# Revit family: Towel_Ring-DXV-Fitzgerald-D35160190_Series
name_source: partatom
category: Specialty Equipment
revit_build: Autodesk Revit 2014 (Build: 20130308_1515(x64)
units: mm (PartAtom-declared; Revit-internal decimal feet)

## types (3) — shared parameters
Assembly Code = C1030220
Default Elevation = 40"
Description = Fitzgerald Towel Ring
Height = 8 1/8"
Installation Type = Wall Mounted
Length = 2 5/8"
Manufacturer = DVX
Price = Prices may vary. Please consult Manufacturer Representative for most up-to-date price list.
Product Documentation Link = https://dxv01.blob.core.windows.net
Product Page URL = https://www.dxv.com
URL = http://www.dxv.com
Warranty Information = Lifetime Limited Warranty
Width = 7 7/16"

## per-type parameters (varying)
| type | Finish | Material |
| D35160190.144 | Metal-DXV-144-Brushed Nickel | Metal-DXV-144-Brushed Nickel |
| D35160190.100 | Metal-DXV-100-Polished Chrome | Metal-DXV-100-Polished Chrome |
| D35160190.150 | Metal-DXV-150-Platinum Nickel | Metal-DXV-150-Platinum Nickel |

note: column(s) folded — value = type name in every type: Model

## geometry (parser evidence)
native form markers: Sweep x3
no freeform markers — native parametric forms only
